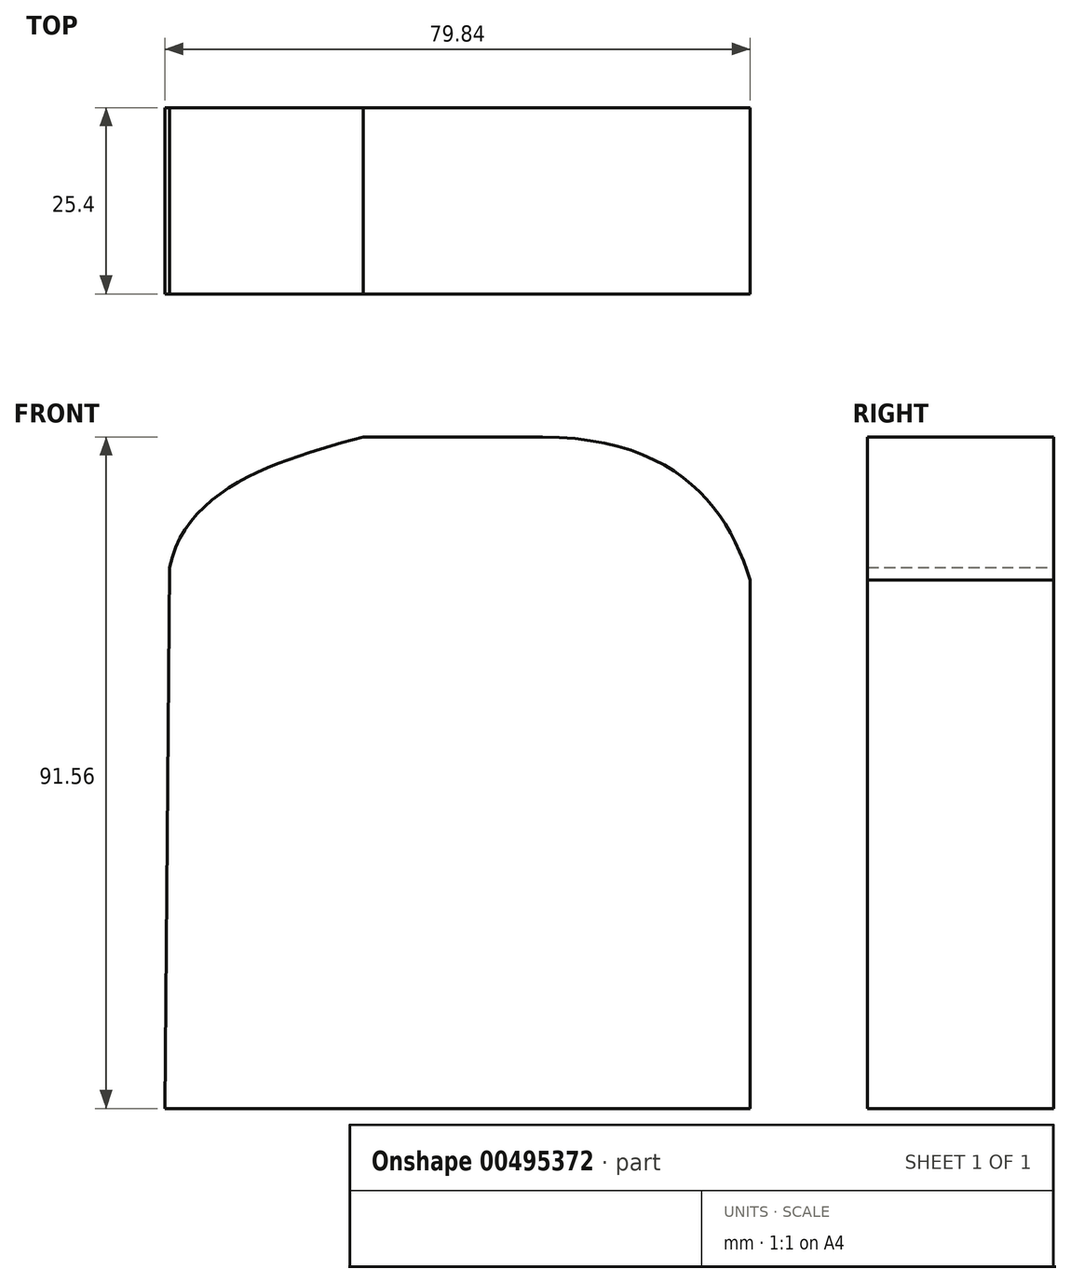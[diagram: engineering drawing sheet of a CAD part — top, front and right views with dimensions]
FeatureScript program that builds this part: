
annotation { "Feature Type Name" : "Feature", "Feature Type Description" : "" }
export const myFeature = defineFeature(function(context is Context, id is Id, definition is map)
    precondition{}
    {
        {
            var Q0;
            Q0=qCreatedBy(makeId("Front.planeOp"),FACE);
            var sketch = newSketch(context, id + "F0", { "sketchPlane" : qUnion([Q0])});
            skLineSegment(sketch, "E0.bottom", {"start": v(-12.86, 66.6) * mm, "end": v(11.61, 66.6) * mm});
            skLineSegment(sketch, "E0.top", {"start": v(-12.86, 47.29) * mm, "end": v(11.61, 47.29) * mm});
            skLineSegment(sketch, "E0.left", {"start": v(-12.86, 66.6) * mm, "end": v(-12.86, 47.29) * mm});
            skLineSegment(sketch, "E0.right", {"start": v(11.61, 66.6) * mm, "end": v(11.61, 47.29) * mm});
            skLineSegment(sketch, "E1.top", {"start": v(-39.92, -44.27) * mm, "end": v(39.92, -44.27) * mm});
            skPoint(sketch, "E1.middle", {"position": v(0, 0.9) * mm});
            skLineSegment(sketch, "E2", {"start": v(-39.26, 29.46) * mm, "end": v(-39.92, -44.27) * mm});
            skLineSegment(sketch, "E3", {"start": v(39.92, 27.76) * mm, "end": v(39.92, -44.27) * mm});
            skFitSpline(sketch, "E4", {"points": [v(-39.26, 29.46) * mm, v(-12.86, 47.29) * mm], "startDerivative": vector(6.73, 33.57) * mm, "endDerivative": vector(32.69, 9) * mm});
            skFitSpline(sketch, "E5", {"points": [v(11.61, 47.29) * mm, v(39.92, 27.76) * mm], "startDerivative": vector(54.13, -0.38) * mm, "endDerivative": vector(9.24, -30.47) * mm});
            skSolve(sketch);
        }
        {
            var Q0;
            Q0=makeQuery(id+"F0.imprint","IMPRINT",FACE,{"disambiguationData":[TD([[makeQuery(id+"F0.imprint","IMPRINT",EDGE,{"derivedFrom":sQuery(id+"F0.wireOp",EDGE,"E0.top")}),-1.0]])]});
            extrude(context, id + "F1", {"entities" : qUnion([Q0]), "depth" : 25.4 * mm});
        }
    });
